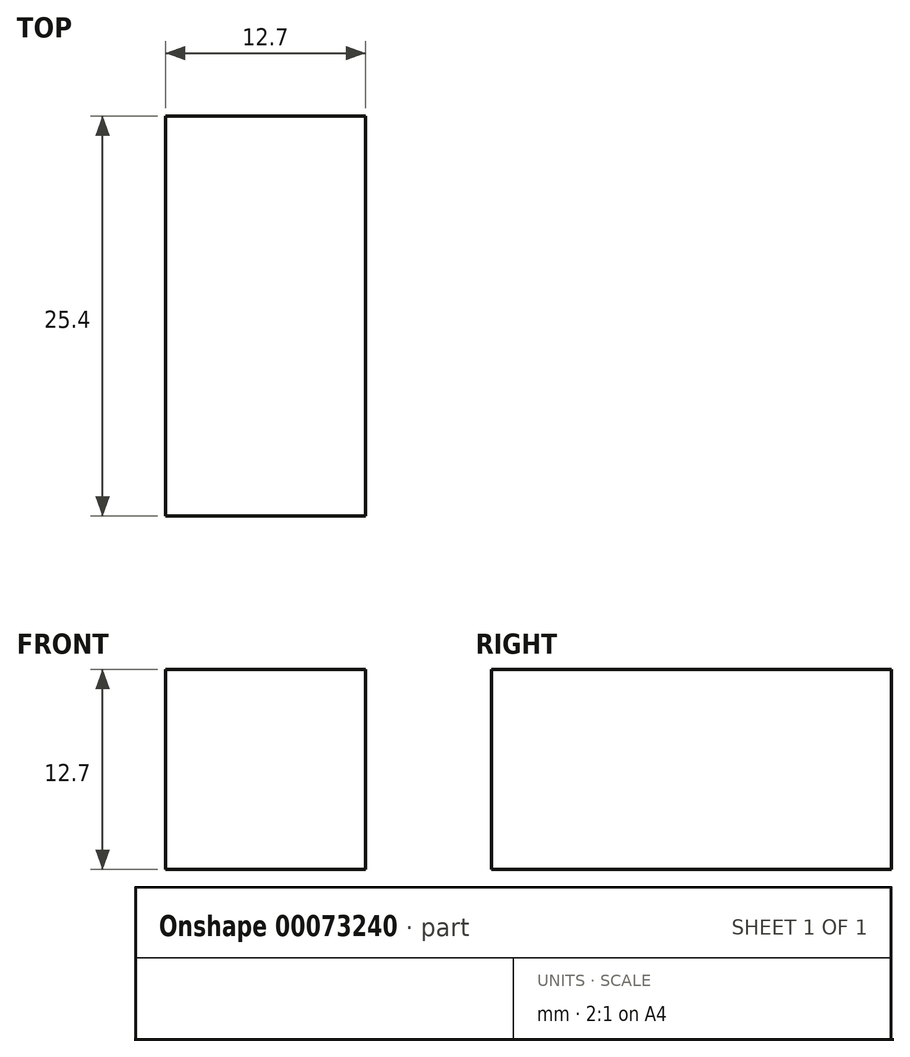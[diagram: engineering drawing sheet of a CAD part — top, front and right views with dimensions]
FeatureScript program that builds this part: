
annotation { "Feature Type Name" : "Feature", "Feature Type Description" : "" }
export const myFeature = defineFeature(function(context is Context, id is Id, definition is map)
    precondition{}
    {
        {
            var Q0;
            Q0=qCreatedBy(makeId("Front.planeOp"),FACE);
            var sketch = newSketch(context, id + "F0", { "sketchPlane" : qUnion([Q0])});
            skLineSegment(sketch, "E0.rect.bottom", {"start": v(6.35, 6.35) * mm, "end": v(-6.35, 6.35) * mm});
            skLineSegment(sketch, "E0.rect.top", {"start": v(6.35, -6.35) * mm, "end": v(-6.35, -6.35) * mm});
            skLineSegment(sketch, "E0.rect.left", {"start": v(6.35, 6.35) * mm, "end": v(6.35, -6.35) * mm});
            skLineSegment(sketch, "E0.rect.right", {"start": v(-6.35, 6.35) * mm, "end": v(-6.35, -6.35) * mm});
            skPoint(sketch, "E0.rect.middle", {"position": v(0, 0) * mm});
            skSolve(sketch);
        }
        {
            var Q0;
            Q0=makeQuery(id+"F0.imprint","IMPRINT",FACE,{"disambiguationData":[TD([[makeQuery(id+"F0.imprint","IMPRINT",EDGE,{"derivedFrom":sQuery(id+"F0.wireOp",EDGE,"E0.rect.bottom")}),1.0]])]});
            extrude(context, id + "F1", {"entities" : qUnion([Q0]), "depth" : 12.7 * mm, "hasSecondDirection" : true, "secondDirectionOppositeDirection" : true, "secondDirectionDepth" : 12.7 * mm});
        }
    });
